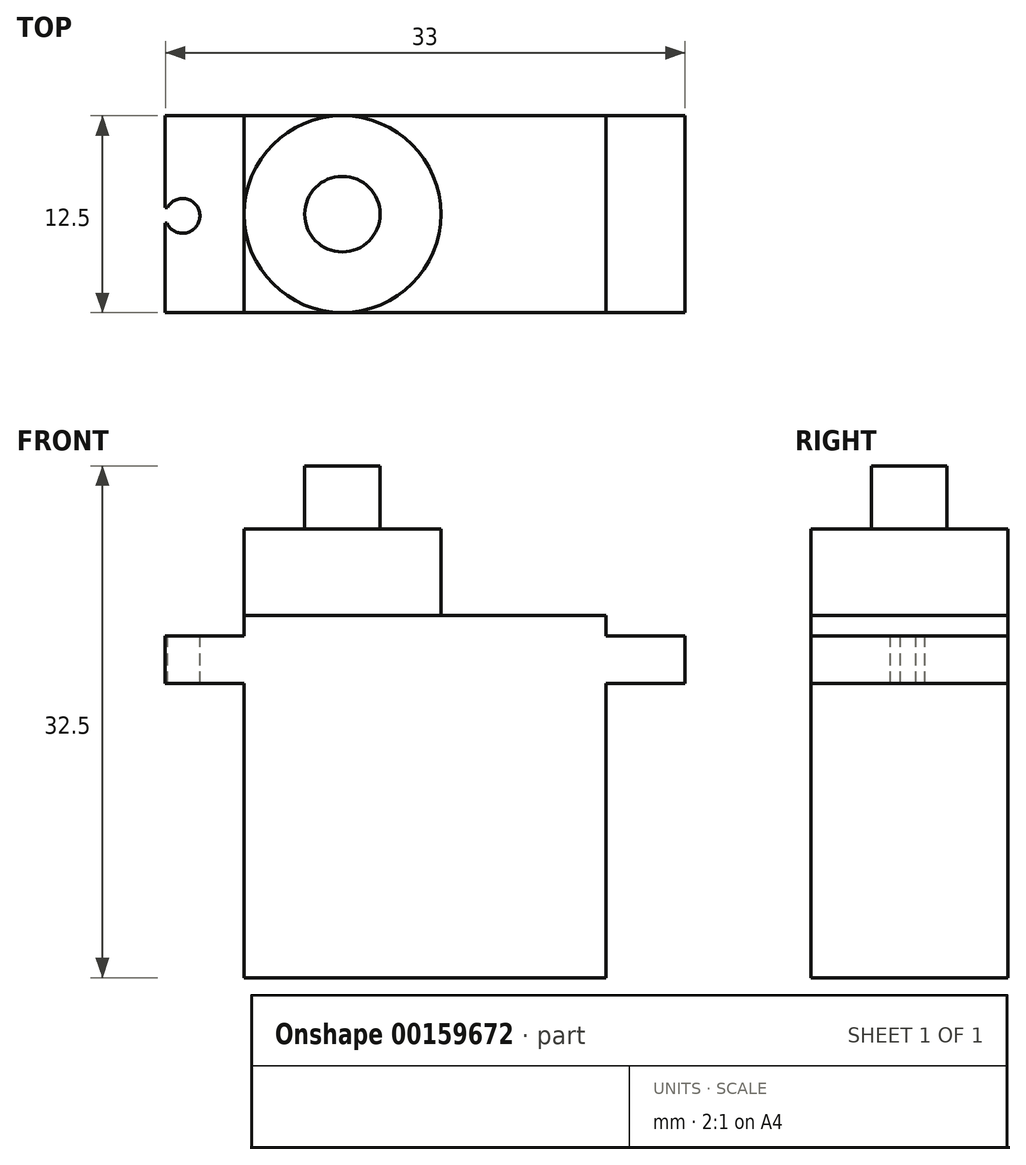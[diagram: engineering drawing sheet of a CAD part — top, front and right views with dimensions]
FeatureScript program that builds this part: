
annotation { "Feature Type Name" : "Feature", "Feature Type Description" : "" }
export const myFeature = defineFeature(function(context is Context, id is Id, definition is map)
    precondition{}
    {
        {
            var Q0;
            Q0=qCreatedBy(makeId("Top.planeOp"),FACE);
            var sketch = newSketch(context, id + "F0", { "sketchPlane" : qUnion([Q0])});
            skLineSegment(sketch, "E0.bottom", {"start": v(-32.91, -7.47) * mm, "end": v(-9.91, -7.47) * mm});
            skLineSegment(sketch, "E0.top", {"start": v(-32.91, -19.97) * mm, "end": v(-9.91, -19.97) * mm});
            skLineSegment(sketch, "E0.left", {"start": v(-32.91, -7.47) * mm, "end": v(-32.91, -19.97) * mm});
            skLineSegment(sketch, "E0.right", {"start": v(-9.91, -7.47) * mm, "end": v(-9.91, -19.97) * mm});
            skSolve(sketch);
        }
        {
            var Q0;
            Q0=makeQuery(id+"F0.imprint","IMPRINT",FACE,{"disambiguationData":[TD([[makeQuery(id+"F0.imprint","IMPRINT",EDGE,{"derivedFrom":sQuery(id+"F0.wireOp",EDGE,"E0.bottom")}),-1.0]])]});
            extrude(context, id + "F1", {"entities" : qUnion([Q0]), "depth" : 23 * mm});
        }
        {
            var Q0;
            Q0=makeQuery(id+"F1.opExtrude","CAP_FACE",FACE,{"disambiguationData":[OSD([sQuery(id+"F0.wireOp",EDGE,"E0.bottom"),sQuery(id+"F0.wireOp",EDGE,"E0.top"),sQuery(id+"F0.wireOp",EDGE,"E0.left"),sQuery(id+"F0.wireOp",EDGE,"E0.right")])],"isStart":false});
            cPlane(context, id + "F2", {"entities" : qUnion([Q0]), "cplaneType" : CPlaneType.OFFSET, "offset" : 1.3 * mm, "oppositeDirection" : true, "width" : 150 * mm, "height" : 150 * mm});
        }
        {
            var Q0;
            Q0=qCreatedBy(id+"F2.planeOp",FACE);
            var sketch = newSketch(context, id + "F3", { "sketchPlane" : qUnion([Q0])});
            skLineSegment(sketch, "E1.bottom", {"start": v(-37.91, -7.47) * mm, "end": v(-4.91, -7.47) * mm});
            skLineSegment(sketch, "E1.top", {"start": v(-37.91, -19.97) * mm, "end": v(-4.91, -19.97) * mm});
            skLineSegment(sketch, "E1.left", {"start": v(-37.91, -7.47) * mm, "end": v(-37.91, -19.97) * mm});
            skLineSegment(sketch, "E1.right", {"start": v(-4.91, -7.47) * mm, "end": v(-4.91, -19.97) * mm});
            skSolve(sketch);
        }
        {
            var Q0;
            Q0=makeQuery(id+"F3.imprint","IMPRINT",FACE,{"disambiguationData":[TD([[makeQuery(id+"F3.imprint","IMPRINT",EDGE,{"derivedFrom":sQuery(id+"F3.wireOp",EDGE,"E1.bottom")}),-1.0]])]});
            extrude(context, id + "F4", {"entities" : qUnion([Q0]), "operationType" : NewBodyOperationType.ADD, "oppositeDirection" : true, "depth" : 3 * mm});
        }
        {
            var Q0;
            Q0=makeQuery(id+"F1.opExtrude","CAP_FACE",FACE,{"disambiguationData":[OSD([sQuery(id+"F0.wireOp",EDGE,"E0.bottom"),sQuery(id+"F0.wireOp",EDGE,"E0.top"),sQuery(id+"F0.wireOp",EDGE,"E0.left"),sQuery(id+"F0.wireOp",EDGE,"E0.right")])],"isStart":false});
            var sketch = newSketch(context, id + "F5", { "sketchPlane" : qUnion([Q0])});
            skCircle(sketch, "E2", {"center": v(-26.66, -13.72) * mm, "radius": 6.25 * mm});
            skSolve(sketch);
        }
        {
            var Q0;
            {var subQ0=sQuery(id+"F5.wireOp",EDGE,"E2");var subQ1=makeQuery(id+"F5.imprint","INTERSECT",VERTEX,{"derivedFrom":[makeQuery(id+"F1.opExtrude","CAP_EDGE",EDGE,{"disambiguationData":[OSD([sQuery(id+"F0.wireOp",EDGE,"E0.left")])],"isStart":false}),subQ0]});Q0=makeQuery(id+"F5.imprint","IMPRINT",FACE,{"disambiguationData":[TD([[makeQuery(id+"F5.imprint","IMPRINT",EDGE,{"disambiguationData":[TD([[subQ1,1.0]])],"derivedFrom":subQ0}),1.0]])]});}
            extrude(context, id + "F6", {"entities" : qUnion([Q0]), "operationType" : NewBodyOperationType.ADD, "depth" : 5.5 * mm});
        }
        {
            var Q0;
            Q0=makeQuery(id+"F6.opExtrude","CAP_FACE",FACE,{"disambiguationData":[OSD([sQuery(id+"F5.wireOp",EDGE,"E2")])],"isStart":false});
            var sketch = newSketch(context, id + "F7", { "sketchPlane" : qUnion([Q0])});
            skCircle(sketch, "E3", {"center": v(-26.66, -13.72) * mm, "radius": 2.4 * mm});
            skSolve(sketch);
        }
        {
            var Q0;
            Q0=makeQuery(id+"F7.imprint","IMPRINT",FACE,{"disambiguationData":[TD([[makeQuery(id+"F7.imprint","IMPRINT",EDGE,{"derivedFrom":sQuery(id+"F7.wireOp",EDGE,"E3")}),1.0]])]});
            extrude(context, id + "F8", {"entities" : qUnion([Q0]), "operationType" : NewBodyOperationType.ADD, "depth" : 4 * mm});
        }
        {
            var Q0;
            {var subQ0=sQuery(id+"F3.wireOp",EDGE,"E1.bottom");var subQ1=sQuery(id+"F3.wireOp",EDGE,"E1.left");var subQ2=sQuery(id+"F3.wireOp",EDGE,"E1.top");Q0=makeQuery(id+"F4.boolean.opBoolean","SPLIT",FACE,{"disambiguationData":[TD([makeQuery(id+"F1.opExtrude","SWEPT_FACE",FACE,{"disambiguationData":[OSD([sQuery(id+"F0.wireOp",EDGE,"E0.left")])]})])],"derivedFrom":makeQuery(id+"F4.opExtrude","CAP_FACE",FACE,{"disambiguationData":[OSD([subQ0,subQ2,subQ1,sQuery(id+"F3.wireOp",EDGE,"E1.right")])],"isStart":true})});}
            var sketch = newSketch(context, id + "F9", { "sketchPlane" : qUnion([Q0])});
            skCircle(sketch, "E4", {"center": v(-36.81, -13.83) * mm, "radius": 1.1 * mm});
            skPoint(sketch, "E5.firstSnap0", {"position": v(-37.91, -13.72) * mm});
            skLineSegment(sketch, "E5.bottom", {"start": v(-38.56, -13.72) * mm, "end": v(-37.14, -13.72) * mm});
            skLineSegment(sketch, "E5.top", {"start": v(-38.56, -13.3) * mm, "end": v(-37.14, -13.3) * mm});
            skLineSegment(sketch, "E5.left", {"start": v(-38.56, -13.72) * mm, "end": v(-38.56, -13.3) * mm});
            skLineSegment(sketch, "E5.right", {"start": v(-37.14, -13.72) * mm, "end": v(-37.14, -13.3) * mm});
            skLineSegment(sketch, "E6.bottom", {"start": v(-35.07, -10.67) * mm, "end": v(-35.6, -10.67) * mm});
            skLineSegment(sketch, "E6.left", {"start": v(-35.07, -10.67) * mm, "end": v(-35.07, -12.06) * mm});
            skLineSegment(sketch, "E6.right", {"start": v(-35.6, -10.67) * mm, "end": v(-35.6, -12.06) * mm});
            skLineSegment(sketch, "E7.top", {"start": v(-38.56, -14.29) * mm, "end": v(-37.14, -14.29) * mm});
            skLineSegment(sketch, "E7.left", {"start": v(-38.56, -13.72) * mm, "end": v(-38.56, -14.29) * mm});
            skLineSegment(sketch, "E7.right", {"start": v(-37.14, -13.72) * mm, "end": v(-37.14, -14.29) * mm});
            skSolve(sketch);
        }
        {
            var Q0;
            Q0 = qSketchRegion(id + "F9", true);
            extrude(context, id + "F10", {"entities" : qUnion([Q0]), "operationType" : NewBodyOperationType.REMOVE, "oppositeDirection" : true, "depth" : 25 * mm});
        }
    });
